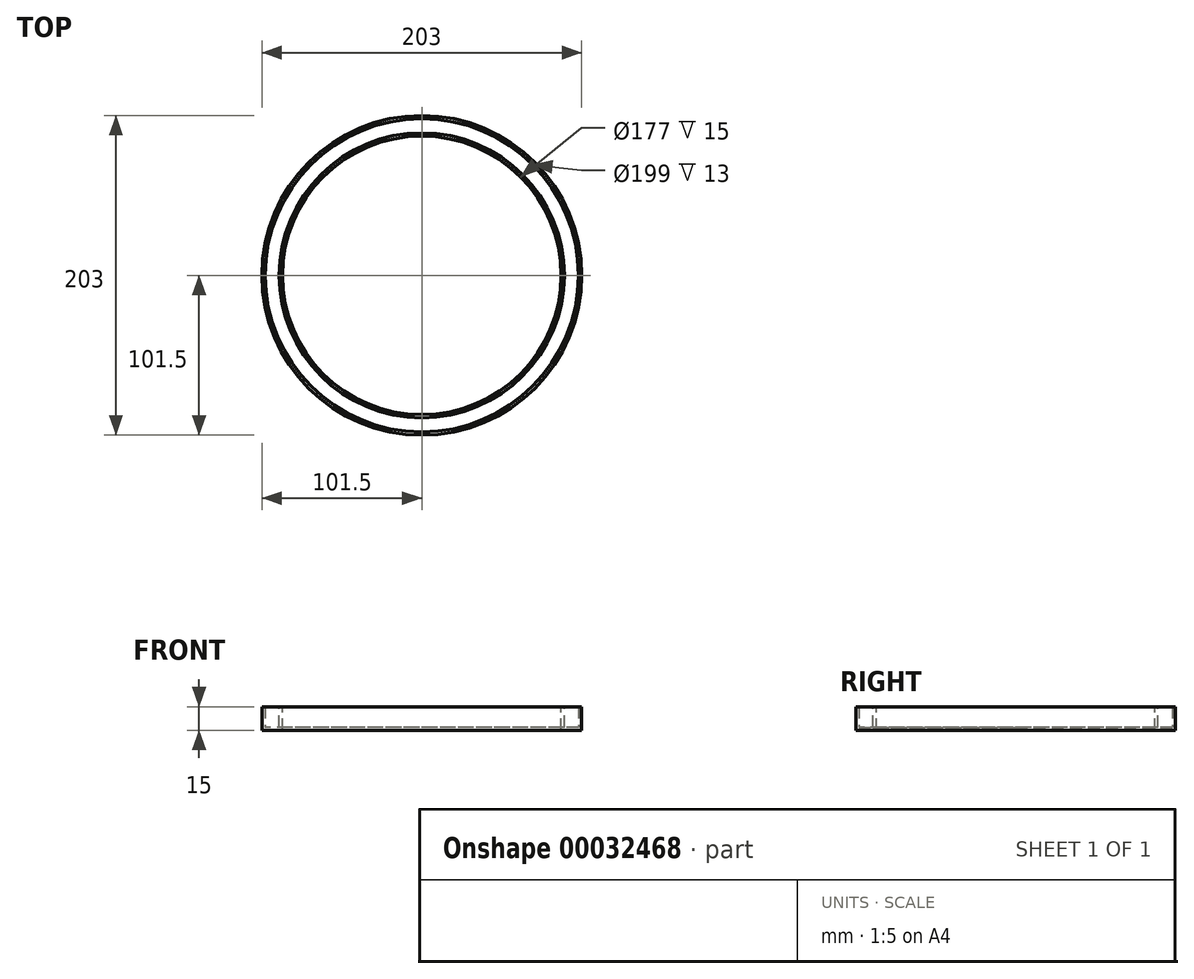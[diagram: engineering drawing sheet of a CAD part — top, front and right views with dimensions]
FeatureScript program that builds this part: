
annotation { "Feature Type Name" : "Feature", "Feature Type Description" : "" }
export const myFeature = defineFeature(function(context is Context, id is Id, definition is map)
    precondition{}
    {
        {
            var Q0;
            Q0=qCreatedBy(makeId("Top.planeOp"),FACE);
            var sketch = newSketch(context, id + "F0", { "sketchPlane" : qUnion([Q0])});
            skCircle(sketch, "E0", {"center": v(0, 0) * mm, "radius": 101.5 * mm});
            skSolve(sketch);
        }
        {
            var Q0;
            Q0=makeQuery(id+"F0.imprint","IMPRINT",FACE,{"disambiguationData":[TD([[makeQuery(id+"F0.imprint","IMPRINT",EDGE,{"derivedFrom":sQuery(id+"F0.wireOp",EDGE,"E0")}),1.0]])]});
            var Q1;
            Q1 = qSketchRegion(id + "F2", true);
            extrude(context, id + "F1", {"entities" : qUnion([Q0, Q1]), "depth" : 15 * mm});
        }
        {
            var Q0;
            Q0=makeQuery(id+"F1.opExtrude","CAP_FACE",FACE,{"disambiguationData":[OSD([sQuery(id+"F0.wireOp",EDGE,"E0")])],"isStart":false});
            var sketch = newSketch(context, id + "F2", { "sketchPlane" : qUnion([Q0])});
            skCircle(sketch, "E1", {"center": v(0, 0) * mm, "radius": 88.5 * mm});
            skSolve(sketch);
        }
        {
            var Q0;
            Q0 = qSketchRegion(id + "F2", true);
            extrude(context, id + "F3", {"entities" : qUnion([Q0]), "operationType" : NewBodyOperationType.REMOVE, "endBound" : BoundingType.THROUGH_ALL, "oppositeDirection" : true, "depth" : 25 * mm});
        }
        {
            var Q0;
            Q0=makeQuery(id+"F1.opExtrude","CAP_FACE",FACE,{"disambiguationData":[OSD([sQuery(id+"F0.wireOp",EDGE,"E0")])],"isStart":false});
            shell(context, id + "F4", {"entities" : qUnion([Q0]), "thickness" : 2 * mm});
        }
    });
